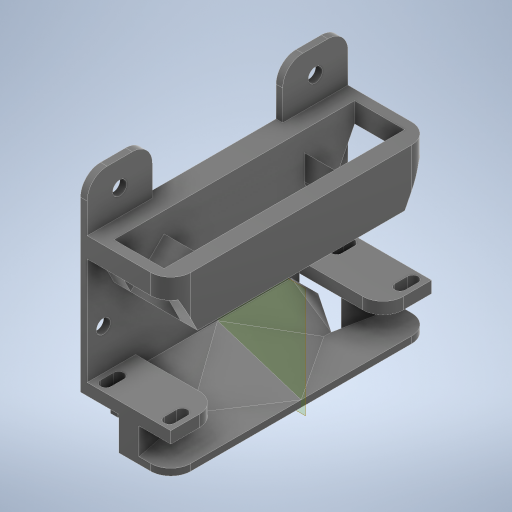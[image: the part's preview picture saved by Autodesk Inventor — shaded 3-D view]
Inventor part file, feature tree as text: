
AUTODESK INVENTOR PART (.ipt)
format: ipt  version: 2024 (Build 280153000, 153)  size: 591,360 bytes
history: native  units: in
note: dims shown in document units (in); Inventor stores cm internally (conversion verified against a paired STEP export)
features: extrude x16, sketch x16, chamfer x5, fillet x5, plane x1
ambient origin geometry x8: Origin, YZ Plane, XZ Plane, XY Plane, X Axis, Y Axis, Z Axis, Center Point
bodies: Solid1 (feature_tree)
feature tree (43):
  extrude  "Extrusion1"  Depth=3.9in
  extrude  "Extrusion2"  TaperAngle=90.0deg  [1 undecoded]
  extrude  "Extrusion7"  TaperAngle=90.0deg  [1 undecoded]
  extrude  "Extrusion8"  TaperAngle=90.0deg  [1 undecoded]
  plane  "Work Plane1"
  extrude  "Extrusion10"  TaperAngle=90.0deg  [1 undecoded]
  chamfer  "Chamfer3"  Distance=0.175in
  chamfer  "Chamfer4"  Distance=0.175in
  extrude  "Extrusion11"  Depth=2.1in
  chamfer  "Chamfer5"  Distance=1.25in
  chamfer  "Chamfer6"  Distance=2.5in
  extrude  "Extrusion12"  Depth=0.25in TaperAngle=45.0deg
  extrude  "Extrusion13"  Depth=3.0in TaperAngle=0.0deg
  extrude  "Extrusion14"  Depth=0.33in TaperAngle=45.0deg
  extrude  "Extrusion15"  Depth=0.33in TaperAngle=45.0deg
  extrude  "Extrusion16"  Depth=3.0in TaperAngle=0.0deg
  fillet  "Fillet1"  Radius=0.15in
  extrude  "Extrusion17"  Depth=0.3in
  chamfer  "Chamfer7"  Distance=0.4in
  extrude  "Extrusion18"  Depth=0.3in TaperAngle=0.0deg
  extrude  "Extrusion19"  Depth=0.75in
  fillet  "Fillet2"  Radius=3.6in
  extrude  "Extrusion20"  Depth=0.3in TaperAngle=0.0deg
  fillet  "Fillet3"  Radius=1.05in
  fillet  "Fillet4"  Radius=2.1in
  extrude  "Extrusion21"  Depth=0.5in
  fillet  "Fillet5"  Radius=0.5in
  sketch  "Sketch1"  dims[d0=1.25in d1=3.9in]
  sketch  "Sketch2"  dims[d2=0.05in d3=90.0deg]
  sketch  "Sketch7"  dims[d4=0.05in d5=90.0deg]
  sketch  "Sketch8"  dims[d6=0.07in d7=90.0deg]
  sketch  "Sketch10"  dims[d8=0.07in d9=90.0deg]
  sketch  "Sketch11"  dims[d10=0.4in]
  sketch  "Sketch12"  dims[d11=0.4in]
  sketch  "Sketch13"  dims[d12=0.08in]
  sketch  "Sketch14"  dims[d13=0.08in d14=0.175in d15=0.0in]
  sketch  "Sketch15"  dims[d16=2.45in d17=0.175in d18=0.0in]
  sketch  "Sketch16"  dims[d19=1.0in d20=2.1in]
  sketch  "Sketch17"  dims[d34=0.1in]
  sketch  "Sketch18"  dims[d35=0.5in d36=1.175in d37=0.0in d38=0.0in]
  sketch  "Sketch19"  dims[d39=0.1in d40=1.25in d41=0.0in d51=2.5in d52=0.0in]
  sketch  "Sketch20"  dims[d53=0.25in d54=1.25in d55=45.0deg d56=0.25in d57=1.25in d58=45.0deg]
  sketch  "Sketch21"  dims[d59=0.6in d60=3.0in d61=0.0in d62=0.33in d63=0.4in d64=45.0deg d65=0.33in d66=0.4in d67=45.0deg d68=3.0in d69=0.0in d70=0.15in d71=0.3in d72=0.4in d73=0.0in d74=0.6in d75=0.0in d76=0.75in d77=3.6in d78=0.3in d79=0.0in d80=1.05in d81=2.1in d82=0.5in d83=0.5in d84=0.5in d85=0.5in d86=0.3in d87=0.0in d88=0.125in d89=0.5in d90=0.0in d91=0.25in d92=0.5in d93=45.0deg d94=0.75in d95=0.0in d96=0.21in d97=0.21in d98=0.4in d99=0.21in d100=0.21in d101=0.75in d102=0.0in d103=0.3in d104=0.1in d105=0.0in d106=0.3in d107=0.3in d108=0.1in d109=0.0in d110=0.3in]
note: 4 required parameter values undecoded (feature->parameter linkage not recoverable at this tier; creation-order binding heuristic only, values carry confidence <= 0.55)
